# Revit family: 101010009209804
name_source: partatom
category: Modelos genéricos
revit_build: Autodesk Revit 2018 (Build: 20190510_1515(x64)
units: mm (PartAtom-declared; Revit-internal decimal feet)

## family parameters
Compartido = No
Corte con vacíos al cargar = No
Cota de conector redondo = Diámetro de uso
Puede alojar armadura = No
Punto de cálculo de habitación = No
Se basa en plano de trabajo = No
Siempre vertical = No
Tipo de pieza = Normal

## types (1)
- SEPARADOR MOLDAJE RUEDA 50MM BOLSA 200UN
    Aplicacion = Se insertan a modo de clip a presión en forma vertical, en elacero de refuerzo estructural (barras), más cercanas al encofrado ó fenólica. (4 Un. x m2 Aprox.)
    Color = Negro
    Descripción = Se usa para distanciar una barra o malla, del encofrado o fenólico.
    Dimension = 50 mm  [stored 0.164042 ft]
    Empresa = CNP SPA.
    Espesor = 0 mm  [stored 0 ft]
    Material = PEAD
    Modelo = SEPARADOR MOLDAJE RUEDA
    Nombre SKU = SEPARADOR MOLDAJE RUEDA 50MM BOLSA 200UN
    Num SKUs = 101010009209804
    URL = https://www.empresascnp.cl
    Unidad = Bolsa 200 Un.
    Url Ficha tecnica = https://empresascnp.cl
    Uso = Para distanciar una barra o malla, del encofrado, y placa de fenólico en muros, en trabajos verticales, y vigas de losa.
    Ventajas = Mantiene un mínimo contacto con el moldaje. Evitan que las barras se curven, desplacen ó se muevan durante el vaciado del hormigón.

note: [stored X ft] marks values corroborated as IEEE doubles in the binary element streams (Revit-internal decimal feet)

## geometry (parser evidence)
native form markers: Sweep x1
no freeform markers — native parametric forms only
